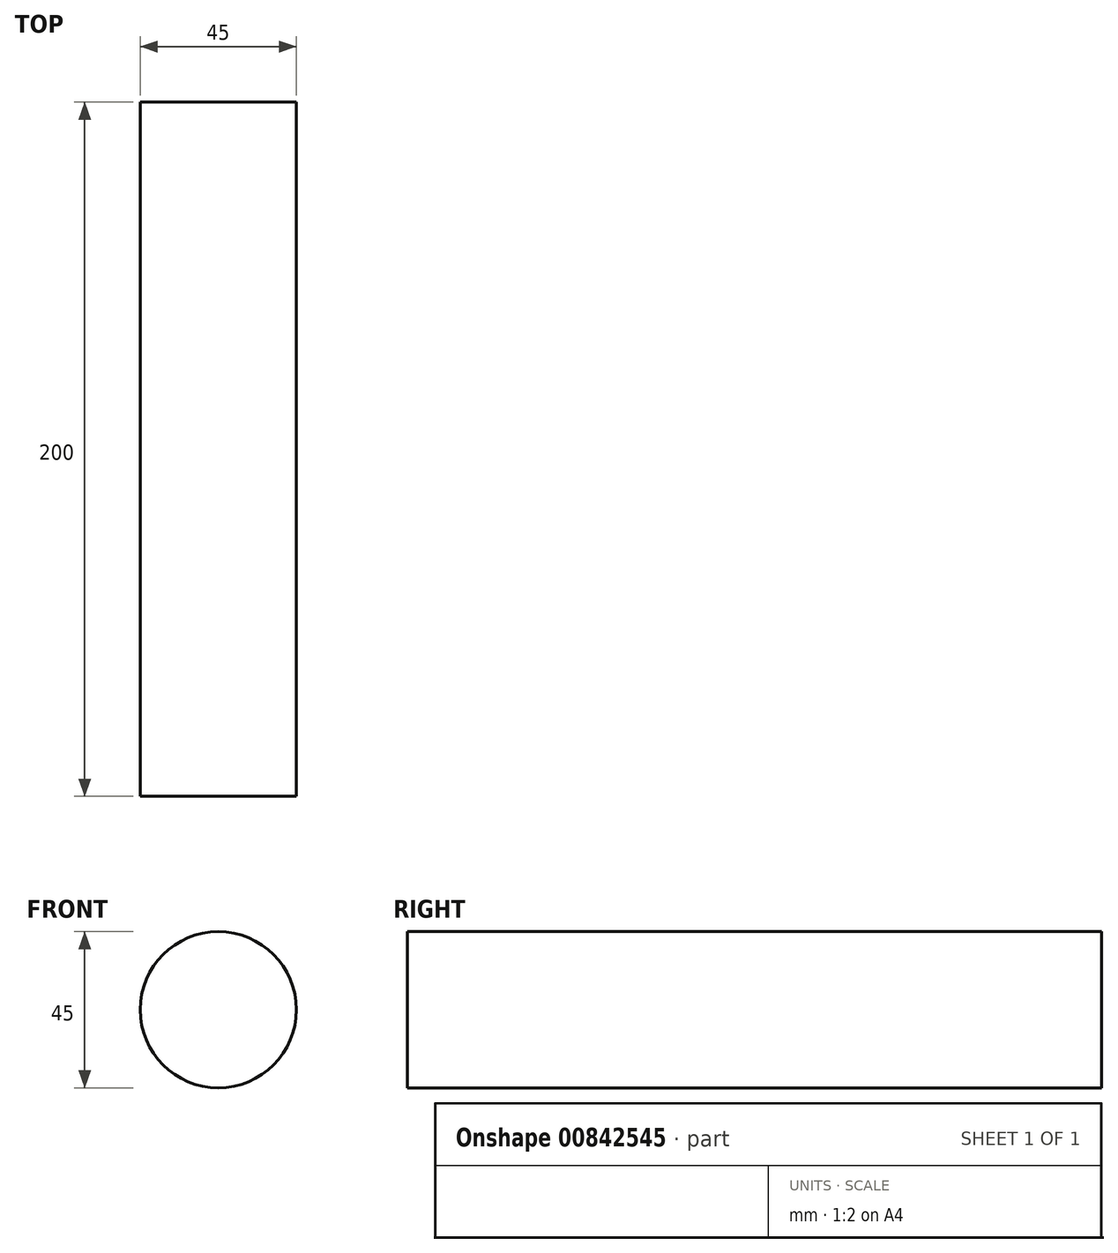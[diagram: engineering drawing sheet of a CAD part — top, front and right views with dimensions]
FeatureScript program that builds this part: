
annotation { "Feature Type Name" : "Feature", "Feature Type Description" : "" }
export const myFeature = defineFeature(function(context is Context, id is Id, definition is map)
    precondition{}
    {
        {
            var Q0;
            Q0=qCreatedBy(makeId("Front.planeOp"),FACE);
            var sketch = newSketch(context, id + "F0", { "sketchPlane" : qUnion([Q0])});
            skCircle(sketch, "E0", {"center": v(0, 0) * mm, "radius": 22.5 * mm});
            skSolve(sketch);
        }
        {
            var Q0;
            Q0 = qSketchRegion(id + "F0", true);
            extrude(context, id + "F1", {"entities" : qUnion([Q0]), "depth" : 200 * mm, "offsetDistance" : 25 * mm});
        }
    });
